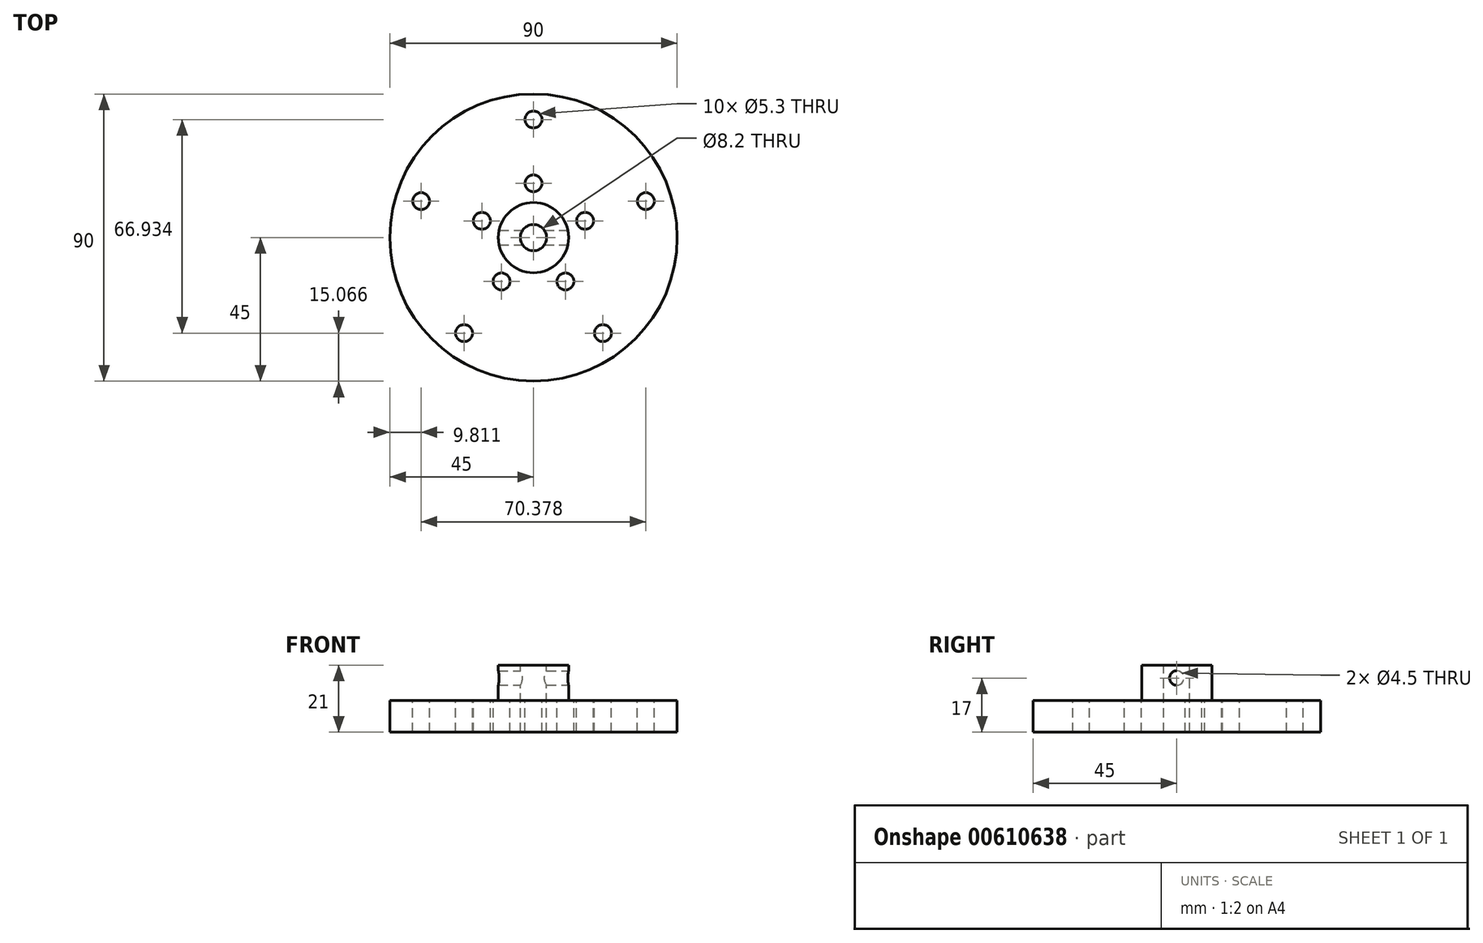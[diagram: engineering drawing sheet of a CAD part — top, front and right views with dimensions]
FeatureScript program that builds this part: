
annotation { "Feature Type Name" : "Feature", "Feature Type Description" : "" }
export const myFeature = defineFeature(function(context is Context, id is Id, definition is map)
    precondition{}
    {
        {
            var Q0;
            Q0=qCreatedBy(makeId("Top.planeOp"),FACE);
            var sketch = newSketch(context, id + "F0", { "sketchPlane" : qUnion([Q0])});
            skCircle(sketch, "E0", {"center": v(0, 0) * mm, "radius": 45 * mm});
            skSolve(sketch);
        }
        {
            var Q0;
            Q0=makeQuery(id+"F0.imprint","IMPRINT",FACE,{"disambiguationData":[TD([[makeQuery(id+"F0.imprint","IMPRINT",EDGE,{"derivedFrom":sQuery(id+"F0.wireOp",EDGE,"E0")}),1.0]])]});
            extrude(context, id + "F1", {"entities" : qUnion([Q0]), "depth" : 10 * mm, "offsetDistance" : 25 * mm});
        }
        {
            var Q0;
            Q0=makeQuery(id+"F1.opExtrude","CAP_FACE",FACE,{"disambiguationData":[OSD([sQuery(id+"F0.wireOp",EDGE,"E0")])],"isStart":false});
            var sketch = newSketch(context, id + "F2", { "sketchPlane" : qUnion([Q0])});
            skCircle(sketch, "E1", {"center": v(0, 0) * mm, "radius": 11 * mm});
            skSolve(sketch);
        }
        {
            var Q0;
            Q0=makeQuery(id+"F2.imprint","IMPRINT",FACE,{"disambiguationData":[TD([[makeQuery(id+"F2.imprint","IMPRINT",EDGE,{"derivedFrom":sQuery(id+"F2.wireOp",EDGE,"E1")}),1.0]])]});
            extrude(context, id + "F3", {"entities" : qUnion([Q0]), "operationType" : NewBodyOperationType.ADD, "depth" : 11 * mm, "offsetDistance" : 25 * mm});
        }
        {
            var Q0;
            Q0=makeQuery(id+"F3.opExtrude","CAP_FACE",FACE,{"disambiguationData":[OSD([sQuery(id+"F2.wireOp",EDGE,"E1")])],"isStart":false});
            var sketch = newSketch(context, id + "F4", { "sketchPlane" : qUnion([Q0])});
            skPoint(sketch, "E2", {"position": v(0, 0) * mm});
            skSolve(sketch);
        }
        {
            var Q0;
            Q0=sQuery(id+"F4.wireOp",VERTEX,"E2");
            var Q1;
            Q1=makeQuery(id+"F1.opExtrude","SWEPT_BODY",BODY,{"disambiguationData":[OSD([sQuery(id+"F0.wireOp",EDGE,"E0")])]});
            hole(context, id + "F5", {"style" : HoleStyle.SIMPLE, "endStyle" : HoleEndStyle.THROUGH, "holeDiameter" : 8.2 * mm, "majorDiameter" : 5 * mm, "tappedDepth" : 12 * mm, "tapClearance" : 3, "locations" : qUnion([Q0]), "scope" : qUnion([Q1])});
        }
        {
            var Q0;
            Q0=makeQuery(id+"F1.opExtrude","CAP_FACE",FACE,{"disambiguationData":[OSD([sQuery(id+"F0.wireOp",EDGE,"E0")])],"isStart":false});
            var sketch = newSketch(context, id + "F6", { "sketchPlane" : qUnion([Q0])});
            skPoint(sketch, "E3", {"position": v(0, 17) * mm});
            skPoint(sketch, "E4.1.0", {"position": v(-16.17, 5.25) * mm});
            skPoint(sketch, "E4.2.0", {"position": v(-10, -13.75) * mm});
            skPoint(sketch, "E4.3.0", {"position": v(10, -13.75) * mm});
            skPoint(sketch, "E4.4.0", {"position": v(16.17, 5.25) * mm});
            skPoint(sketch, "E4.center", {"position": v(0, 0) * mm});
            skPoint(sketch, "E5", {"position": v(0, 37) * mm});
            skPoint(sketch, "E6.1.0", {"position": v(-35.19, 11.43) * mm});
            skPoint(sketch, "E6.2.0", {"position": v(-21.75, -29.93) * mm});
            skPoint(sketch, "E6.3.0", {"position": v(21.75, -29.93) * mm});
            skPoint(sketch, "E6.4.0", {"position": v(35.19, 11.43) * mm});
            skSolve(sketch);
        }
        {
            var Q0;
            Q0=sQuery(id+"F6.wireOp",VERTEX,"E3");
            var Q1;
            Q1=sQuery(id+"F6.wireOp",VERTEX,"E4.5.0");
            var Q2;
            Q2=sQuery(id+"F6.wireOp",VERTEX,"E4.4.0");
            var Q3;
            Q3=sQuery(id+"F6.wireOp",VERTEX,"E4.3.0");
            var Q4;
            Q4=sQuery(id+"F6.wireOp",VERTEX,"E4.2.0");
            var Q5;
            Q5=sQuery(id+"F6.wireOp",VERTEX,"E4.1.0");
            var Q6;
            Q6=sQuery(id+"F6.wireOp",VERTEX,"E6.4.0");
            var Q7;
            Q7=sQuery(id+"F6.wireOp",VERTEX,"E6.3.0");
            var Q8;
            Q8=sQuery(id+"F6.wireOp",VERTEX,"E6.2.0");
            var Q9;
            Q9=sQuery(id+"F6.wireOp",VERTEX,"E6.1.0");
            var Q10;
            Q10=sQuery(id+"F6.wireOp",VERTEX,"E5");
            var Q11;
            Q11=makeQuery(id+"F1.opExtrude","SWEPT_BODY",BODY,{"disambiguationData":[OSD([sQuery(id+"F0.wireOp",EDGE,"E0")])]});
            hole(context, id + "F7", {"style" : HoleStyle.SIMPLE, "endStyle" : HoleEndStyle.THROUGH, "holeDiameter" : 5.3 * mm, "majorDiameter" : 5 * mm, "tappedDepth" : 12 * mm, "tapClearance" : 3, "locations" : qUnion([Q0, Q1, Q2, Q3, Q4, Q5, Q6, Q7, Q8, Q9, Q10]), "scope" : qUnion([Q11])});
        }
        {
            var Q0;
            Q0=qCreatedBy(makeId("Right.planeOp"),FACE);
            var sketch = newSketch(context, id + "F8", { "sketchPlane" : qUnion([Q0])});
            skCircle(sketch, "E7", {"center": v(0, 17) * mm, "radius": 2.25 * mm});
            skSolve(sketch);
        }
        {
            var Q0;
            Q0=qSketchRegion(id+"F8",true);
            extrude(context, id + "F9", {"entities" : qUnion([Q0]), "operationType" : NewBodyOperationType.REMOVE, "endBound" : BoundingType.SYMMETRIC, "oppositeDirection" : true, "depth" : 100 * mm, "offsetDistance" : 25 * mm});
        }
    });
